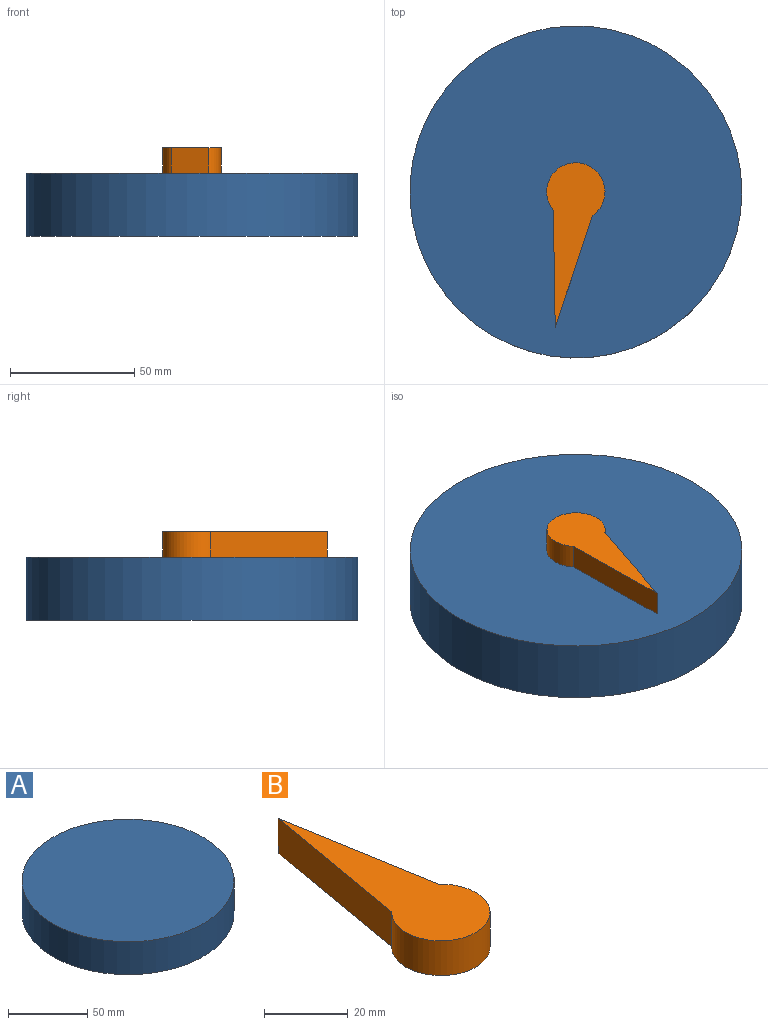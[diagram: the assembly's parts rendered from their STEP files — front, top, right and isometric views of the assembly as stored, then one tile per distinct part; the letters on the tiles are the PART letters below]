
ASSEMBLY  parts=2 mates=1
PART A: 3 faces, bbox 133.7x133.7x25.4 mm
  f0: cylinder r=66.84mm len=133.67mm, axis (0,0,-1), area 10666.7mm2, adj f1,f2
  f1: plane 133.67x133.67mm, normal (0,0,1), area 14034mm2, adj f0
  f2: plane 133.67x133.67mm, normal (0,0,-1), area 14034mm2, adj f0
PART B: 5 faces, bbox 23.5x66.8x10.2 mm
  f0: plane 46.58x10.16mm, normal (-0.99,0.17,0), area 480.4mm2, adj f1,f2,f3,f4
  f1: cylinder r=11.74mm len=23.49mm, axis (0,0,-1), area 571.3mm2, adj f0,f2,f3,f4
  f2: plane 46.31x10.16mm, normal (0.99,0.17,0), area 477.2mm2, adj f0,f1,f3,f4
  f3: plane 66.8x23.49mm, normal (0,0,1), area 769.5mm2, adj f0,f1,f2
  f4: plane 66.8x23.49mm, normal (0,0,-1), area 769.5mm2, adj f0,f1,f2
PLACE A t=(1.02,-5.53,-26.96)mm fixed
PLACE B rot(axis=(0,0,1),171.3deg) t=(1.02,-5.53,-26.96)mm
MATE revolute A.f0 <-> B.f1  axis (0,0,1) through (1.02,-5.53,-1.56)mm
